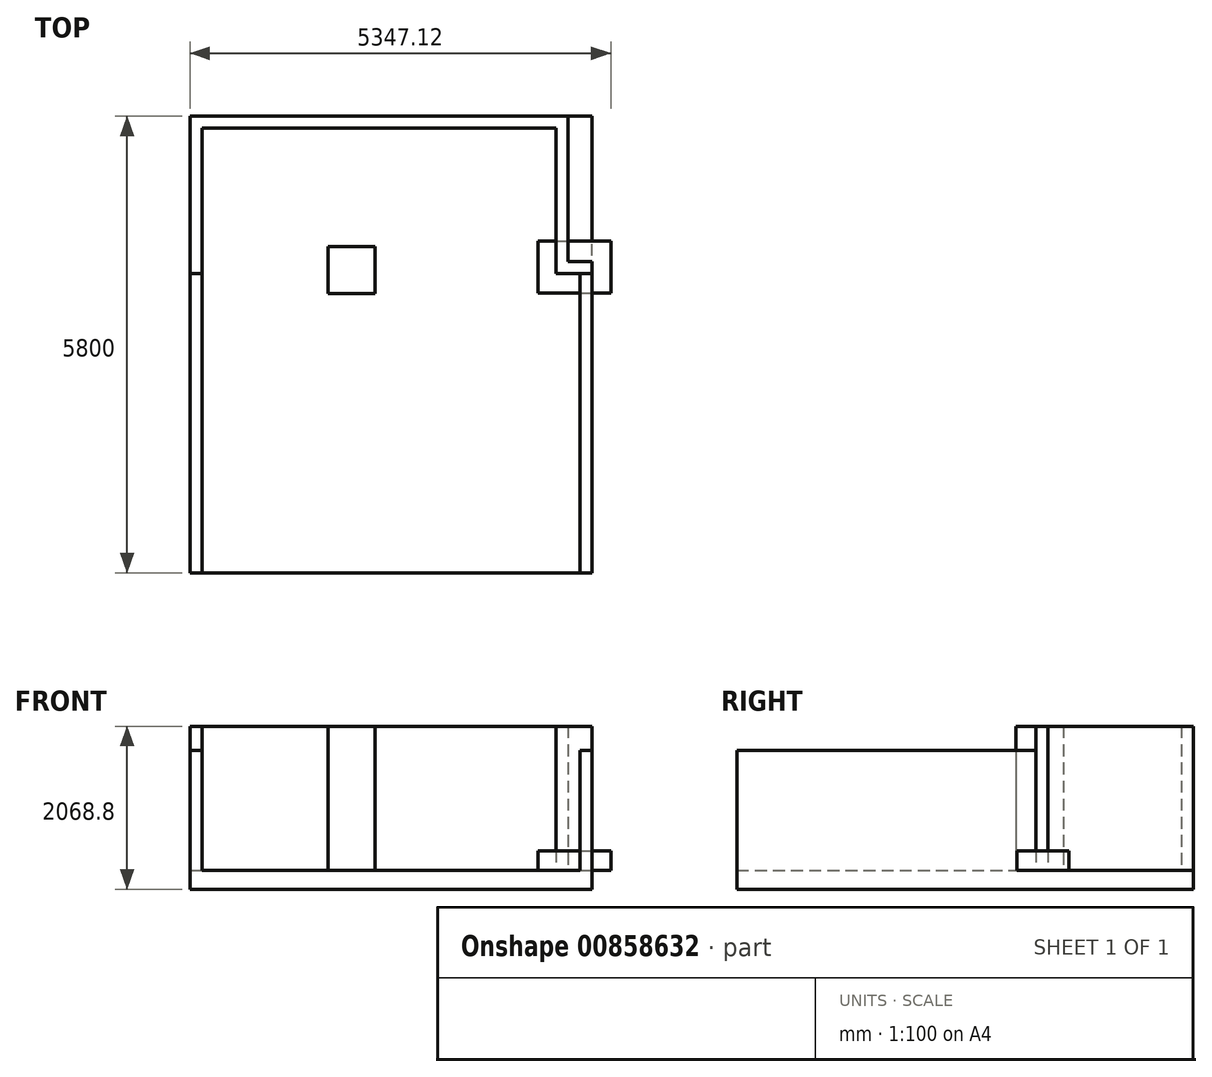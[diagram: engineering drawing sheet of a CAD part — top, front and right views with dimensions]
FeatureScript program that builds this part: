
annotation { "Feature Type Name" : "Feature", "Feature Type Description" : "" }
export const myFeature = defineFeature(function(context is Context, id is Id, definition is map)
    precondition{}
    {
        {
            var Q0;
            Q0=qCreatedBy(makeId("Top.planeOp"),FACE);
            var sketch = newSketch(context, id + "F0", { "sketchPlane" : qUnion([Q0])});
            skLineSegment(sketch, "E0.bottom", {"start": v(-2552.4, -1900) * mm, "end": v(-2400, -1900) * mm});
            skLineSegment(sketch, "E0.top", {"start": v(-2552.4, 1900) * mm, "end": v(-2400, 1900) * mm});
            skLineSegment(sketch, "E0.left", {"start": v(-2552.4, -1900) * mm, "end": v(-2552.4, 1900) * mm});
            skLineSegment(sketch, "E0.right", {"start": v(-2400, -1900) * mm, "end": v(-2400, 1900) * mm});
            skPoint(sketch, "E0.middle", {"position": v(-2476.2, 0) * mm});
            skLineSegment(sketch, "E1", {"start": v(0, 1900) * mm, "end": v(0, -1900) * mm, "construction": true});
            skLineSegment(sketch, "E2.MirrorCS", {"start": v(2552.4, 1900) * mm, "end": v(2400, 1900) * mm});
            skLineSegment(sketch, "E3.MirrorCS", {"start": v(2552.4, -1900) * mm, "end": v(2400, -1900) * mm});
            skLineSegment(sketch, "E4.MirrorCS", {"start": v(2400, -1900) * mm, "end": v(2400, 1900) * mm});
            skLineSegment(sketch, "E5.MirrorCS", {"start": v(2552.4, -1900) * mm, "end": v(2552.4, 1900) * mm});
            skPoint(sketch, "E6.MirrorP", {"position": v(2476.2, 0) * mm});
            skSolve(sketch);
        }
        {
            var Q0;
            Q0 = qSketchRegion(id + "F0", true);
            extrude(context, id + "F1", {"entities" : qUnion([Q0]), "depth" : 1524 * mm, "offsetDistance" : 25 * mm});
        }
        {
            var Q0;
            Q0=makeQuery(id+"F1.opExtrude","CAP_FACE",FACE,{"disambiguationData":[OSD([sQuery(id+"F0.wireOp",EDGE,"E0.bottom"),sQuery(id+"F0.wireOp",EDGE,"E0.top"),sQuery(id+"F0.wireOp",EDGE,"E0.left"),sQuery(id+"F0.wireOp",EDGE,"E0.right")])],"isStart":true});
            var sketch = newSketch(context, id + "F2", { "sketchPlane" : qUnion([Q0])});
            skLineSegment(sketch, "E7.bottom", {"start": v(-2552.4, 1900) * mm, "end": v(2552.4, 1900) * mm});
            skLineSegment(sketch, "E7.top", {"start": v(-2552.4, -1900) * mm, "end": v(2552.4, -1900) * mm});
            skLineSegment(sketch, "E7.left", {"start": v(-2552.4, 1900) * mm, "end": v(-2552.4, -1900) * mm});
            skLineSegment(sketch, "E7.right", {"start": v(2552.4, 1900) * mm, "end": v(2552.4, -1900) * mm});
            skPoint(sketch, "E8.0", {"position": v(2552.4, -1900) * mm});
            skSolve(sketch);
        }
        {
            var Q0;
            Q0 = qSketchRegion(id + "F2", true);
            extrude(context, id + "F3", {"entities" : qUnion([Q0]), "depth" : 240 * mm, "offsetDistance" : 25 * mm});
        }
        {
            var Q0;
            Q0=makeQuery(id+"F3.opExtrude","CAP_FACE",FACE,{"disambiguationData":[OSD([sQuery(id+"F2.wireOp",EDGE,"E7.bottom"),sQuery(id+"F2.wireOp",EDGE,"E7.top"),sQuery(id+"F2.wireOp",EDGE,"E7.left"),sQuery(id+"F2.wireOp",EDGE,"E7.right")])],"isStart":false});
            var sketch = newSketch(context, id + "F4", { "sketchPlane" : qUnion([Q0])});
            skLineSegment(sketch, "E9.bottom", {"start": v(-2552.4, -1900) * mm, "end": v(2552.4, -1900) * mm});
            skLineSegment(sketch, "E9.top", {"start": v(-2552.4, -3900) * mm, "end": v(2552.4, -3900) * mm});
            skLineSegment(sketch, "E9.left", {"start": v(-2552.4, -1900) * mm, "end": v(-2552.4, -3900) * mm});
            skLineSegment(sketch, "E9.right", {"start": v(2552.4, -1900) * mm, "end": v(2552.4, -3900) * mm});
            skSolve(sketch);
        }
        {
            var Q0;
            Q0=makeQuery(id+"F4.imprint","IMPRINT",FACE,{"disambiguationData":[TD([[makeQuery(id+"F4.imprint","IMPRINT",EDGE,{"derivedFrom":sQuery(id+"F4.wireOp",EDGE,"E9.bottom")}),-1.0]])]});
            var Q1;
            Q1=makeQuery(id+"F3.opExtrude","CAP_FACE",FACE,{"disambiguationData":[OSD([sQuery(id+"F2.wireOp",EDGE,"E7.bottom"),sQuery(id+"F2.wireOp",EDGE,"E7.top"),sQuery(id+"F2.wireOp",EDGE,"E7.left"),sQuery(id+"F2.wireOp",EDGE,"E7.right")])],"isStart":true});
            extrude(context, id + "F5", {"entities" : qUnion([Q0]), "operationType" : NewBodyOperationType.ADD, "endBound" : BoundingType.UP_TO_SURFACE, "oppositeDirection" : true, "depth" : 25 * mm, "endBoundEntityFace" : qUnion([Q1]), "offsetDistance" : 25 * mm});
        }
        {
            var Q0;
            {var subQ0=sQuery(id+"F2.wireOp",EDGE,"E7.right");var subQ1=sQuery(id+"F2.wireOp",EDGE,"E7.left");var subQ2=sQuery(id+"F2.wireOp",EDGE,"E7.top");var subQ3=sQuery(id+"F2.wireOp",EDGE,"E7.bottom");Q0=makeQuery(id+"F5.boolean.opBoolean","MERGE",FACE,{"derivedFrom":[makeQuery(id+"F3.opExtrude","CAP_FACE",FACE,{"disambiguationData":[OSD([subQ3,subQ2,subQ1,subQ0])],"isStart":true}),makeQuery(id+"F5.opExtrude","CAP_FACE",FACE,{"disambiguationData":[OSD([subQ3,subQ2,subQ1,subQ0])],"isStart":false})]});}
            var sketch = newSketch(context, id + "F6", { "sketchPlane" : qUnion([Q0])});
            skLineSegment(sketch, "E10.bottom", {"start": v(1871, 1656.28) * mm, "end": v(2794.72, 1656.28) * mm});
            skLineSegment(sketch, "E10.top", {"start": v(1871, 2314.97) * mm, "end": v(2794.72, 2314.97) * mm});
            skLineSegment(sketch, "E10.left", {"start": v(1871, 1656.28) * mm, "end": v(1871, 2314.97) * mm});
            skLineSegment(sketch, "E10.right", {"start": v(2794.72, 1656.28) * mm, "end": v(2794.72, 2314.97) * mm});
            skSolve(sketch);
        }
        {
            var Q0;
            {var subQ0=sQuery(id+"F6.wireOp",EDGE,"E10.right");Q0=makeQuery(id+"F6.imprint","IMPRINT",FACE,{"disambiguationData":[TD([[makeQuery(id+"F6.imprint","IMPRINT",EDGE,{"derivedFrom":subQ0}),1.0]])]});}
            var Q1;
            {var subQ0=sQuery(id+"F6.wireOp",EDGE,"E10.left");Q1=makeQuery(id+"F6.imprint","IMPRINT",FACE,{"disambiguationData":[TD([[makeQuery(id+"F6.imprint","IMPRINT",EDGE,{"derivedFrom":subQ0}),-1.0]])]});}
            extrude(context, id + "F7", {"entities" : qUnion([Q0, Q1]), "depth" : 250 * mm, "offsetDistance" : 25 * mm});
        }
        {
            var Q0;
            {var subQ0=sQuery(id+"F2.wireOp",EDGE,"E7.right");var subQ1=sQuery(id+"F2.wireOp",EDGE,"E7.left");var subQ2=sQuery(id+"F2.wireOp",EDGE,"E7.top");var subQ3=sQuery(id+"F2.wireOp",EDGE,"E7.bottom");Q0=makeQuery(id+"F5.boolean.opBoolean","MERGE",FACE,{"derivedFrom":[makeQuery(id+"F3.opExtrude","CAP_FACE",FACE,{"disambiguationData":[OSD([subQ3,subQ2,subQ1,subQ0])],"isStart":true}),makeQuery(id+"F5.opExtrude","CAP_FACE",FACE,{"disambiguationData":[OSD([subQ3,subQ2,subQ1,subQ0])],"isStart":false})]});}
            var sketch = newSketch(context, id + "F8", { "sketchPlane" : qUnion([Q0])});
            skLineSegment(sketch, "E11.bottom", {"start": v(-2552.4, 1900) * mm, "end": v(-2400, 1900) * mm});
            skLineSegment(sketch, "E11.top", {"start": v(-2552.4, 3900) * mm, "end": v(-2400, 3900) * mm});
            skLineSegment(sketch, "E11.left", {"start": v(-2552.4, 1900) * mm, "end": v(-2552.4, 3900) * mm});
            skLineSegment(sketch, "E11.right", {"start": v(-2400, 1900) * mm, "end": v(-2400, 3900) * mm});
            skPoint(sketch, "E12.0", {"position": v(-2400, 1900) * mm});
            skLineSegment(sketch, "E13.bottom", {"start": v(2095.2, 1900) * mm, "end": v(2247.6, 1900) * mm});
            skLineSegment(sketch, "E13.top", {"start": v(2095.2, 3900) * mm, "end": v(2247.6, 3900) * mm});
            skLineSegment(sketch, "E13.left", {"start": v(2095.2, 1900) * mm, "end": v(2095.2, 3900) * mm});
            skLineSegment(sketch, "E13.right", {"start": v(2247.6, 1900) * mm, "end": v(2247.6, 3900) * mm});
            skPoint(sketch, "E14.0", {"position": v(2095.2, 1900) * mm});
            skLineSegment(sketch, "E15.bottom", {"start": v(-2400, 3900) * mm, "end": v(2095.2, 3900) * mm});
            skLineSegment(sketch, "E15.top", {"start": v(-2400, 3747.6) * mm, "end": v(2095.2, 3747.6) * mm});
            skLineSegment(sketch, "E15.left", {"start": v(-2400, 3900) * mm, "end": v(-2400, 3747.6) * mm});
            skLineSegment(sketch, "E15.right", {"start": v(2095.2, 3900) * mm, "end": v(2095.2, 3747.6) * mm});
            skLineSegment(sketch, "E16.bottom", {"start": v(2247.6, 1900) * mm, "end": v(2552.4, 1900) * mm});
            skLineSegment(sketch, "E16.top", {"start": v(2247.6, 2052.4) * mm, "end": v(2552.4, 2052.4) * mm});
            skLineSegment(sketch, "E16.left", {"start": v(2247.6, 1900) * mm, "end": v(2247.6, 2052.4) * mm});
            skLineSegment(sketch, "E16.right", {"start": v(2552.4, 1900) * mm, "end": v(2552.4, 2052.4) * mm});
            skSolve(sketch);
        }
        {
            var Q0;
            Q0 = qSketchRegion(id + "F8", true);
            extrude(context, id + "F9", {"entities" : qUnion([Q0]), "depth" : 1828.8 * mm, "offsetDistance" : 25 * mm});
        }
        {
            var Q0;
            {var subQ0=sQuery(id+"F2.wireOp",EDGE,"E7.right");var subQ1=sQuery(id+"F2.wireOp",EDGE,"E7.left");var subQ2=sQuery(id+"F2.wireOp",EDGE,"E7.top");var subQ3=sQuery(id+"F2.wireOp",EDGE,"E7.bottom");Q0=makeQuery(id+"F5.boolean.opBoolean","MERGE",FACE,{"derivedFrom":[makeQuery(id+"F3.opExtrude","CAP_FACE",FACE,{"disambiguationData":[OSD([subQ3,subQ2,subQ1,subQ0])],"isStart":true}),makeQuery(id+"F5.opExtrude","CAP_FACE",FACE,{"disambiguationData":[OSD([subQ3,subQ2,subQ1,subQ0])],"isStart":false})]});}
            var sketch = newSketch(context, id + "F10", { "sketchPlane" : qUnion([Q0])});
            skLineSegment(sketch, "E17.bottom", {"start": v(-200, 2247.6) * mm, "end": v(-800, 2247.6) * mm});
            skLineSegment(sketch, "E17.top", {"start": v(-200, 1647.6) * mm, "end": v(-800, 1647.6) * mm});
            skLineSegment(sketch, "E17.left", {"start": v(-200, 2247.6) * mm, "end": v(-200, 1647.6) * mm});
            skLineSegment(sketch, "E17.right", {"start": v(-800, 2247.6) * mm, "end": v(-800, 1647.6) * mm});
            skSolve(sketch);
        }
        {
            var Q0;
            Q0=makeQuery(id+"F10.imprint","IMPRINT",FACE,{"disambiguationData":[TD([[makeQuery(id+"F10.imprint","IMPRINT",EDGE,{"derivedFrom":sQuery(id+"F10.wireOp",EDGE,"E17.bottom")}),1.0]])]});
            var Q1;
            Q1=makeQuery(id+"F9.opExtrude","CAP_FACE",FACE,{"disambiguationData":[OSD([sQuery(id+"F8.wireOp",EDGE,"E11.bottom"),sQuery(id+"F8.wireOp",EDGE,"E11.top"),sQuery(id+"F8.wireOp",EDGE,"E11.left"),sQuery(id+"F8.wireOp",EDGE,"E11.right"),sQuery(id+"F8.wireOp",EDGE,"E13.bottom"),sQuery(id+"F8.wireOp",EDGE,"E13.top"),sQuery(id+"F8.wireOp",EDGE,"E13.left"),sQuery(id+"F8.wireOp",EDGE,"E13.right"),sQuery(id+"F8.wireOp",EDGE,"E15.bottom"),sQuery(id+"F8.wireOp",EDGE,"E15.top"),sQuery(id+"F8.wireOp",EDGE,"E16.bottom"),sQuery(id+"F8.wireOp",EDGE,"E16.top"),sQuery(id+"F8.wireOp",EDGE,"E16.right")])],"isStart":false});
            extrude(context, id + "F11", {"entities" : qUnion([Q0]), "operationType" : NewBodyOperationType.ADD, "endBound" : BoundingType.UP_TO_SURFACE, "depth" : 25 * mm, "endBoundEntityFace" : qUnion([Q1]), "offsetDistance" : 25 * mm});
        }
    });
